# Revit family: Building-ContenitoriIncasso-GEWISS-24SC-TORRETTE-SCOMPARSA_CASSEFORME
name_source: partatom
category: Apparecchi elettrici
revit_build: Autodesk Revit 2016 (Build: 20161004_0715(x64)
units: mm (PartAtom-declared; Revit-internal decimal feet)

## family parameters
Condiviso = Sì
Host = Superficie
Mantenere orientamento annotazione = Sì
Punto di calcolo locali = Sì
Quota connettore circolare = Usa diametro
Taglio con vuoti quando caricato = Sì
Tipo di parte = Normale

## types (2) — shared parameters
Catalogo = BUILDING
Catalogo Serie = 24SC
Codice Electrocod = 200
IDF = dde60852-3545-4396-b662-6cfd727f457d
IDT = eb2e272e-e186-4efe-a574-cdabb52c6024
Immagine tipo = GW24622.jpg
Materiale = Metallo
Produttore = GEWISS S.p.A.
Prospetto di default = 1219 mm
SEO = Cassaforma
Scheda Tecnica = https://www.gewiss.com
Tipo = Torrette a Scomparsa Casseforme_GENERICO : GW24622 Cassaforma in metallo per torretta 20-32p
URL = https://www.gewiss.com
Versione file RFA = 19.0

## per-type parameters (varying)
| type | Adatto per torrette | Codice EAN | Descrizione | Modello |
| GW24622 - Cassaforma in metallo per torretta 20-32p | GW24602, GW24612 | 8011564759664 | CASSAFORMA IN METALLO P. TORRETTA 20-32P | GW24622 |
| GW24621 - Cassaforma in metallo per torretta 10-16p | GW24601, GW24611 | 8011564759657 | CASSAFORMA IN METALLO P.TORRETTA 10-16P | GW24621 |

## geometry (parser evidence)
native form markers: Blend x2, Sweep x2
no freeform markers — native parametric forms only
